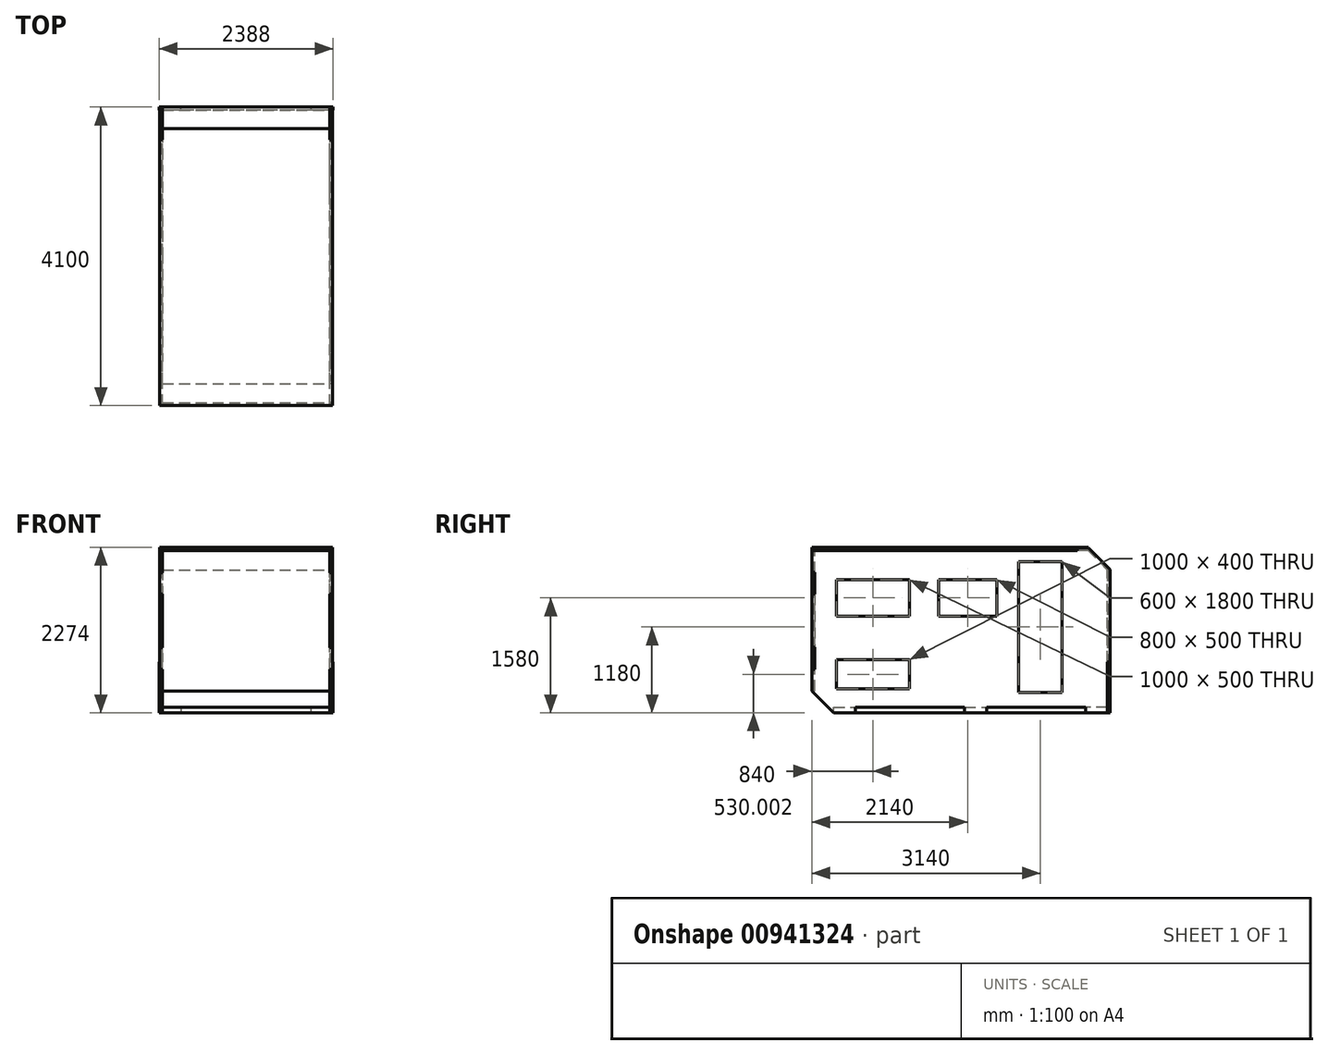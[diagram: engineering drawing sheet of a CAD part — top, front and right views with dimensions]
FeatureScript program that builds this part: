
annotation { "Feature Type Name" : "Feature", "Feature Type Description" : "" }
export const myFeature = defineFeature(function(context is Context, id is Id, definition is map)
    precondition{}
    {
        {
            var Q0;
            Q0=qCreatedBy(makeId("Front.planeOp"),FACE);
            var sketch = newSketch(context, id + "F0", { "sketchPlane" : qUnion([Q0])});
            skLineSegment(sketch, "E0", {"start": v(2175.17, -88.34) * mm, "end": v(1875.17, -88.34) * mm});
            skLineSegment(sketch, "E1", {"start": v(1875.17, -88.34) * mm, "end": v(1875.17, -8.34) * mm});
            skLineSegment(sketch, "E2", {"start": v(1875.17, -8.34) * mm, "end": v(87.17, -8.34) * mm});
            skLineSegment(sketch, "E3", {"start": v(87.17, -8.34) * mm, "end": v(87.17, -88.34) * mm});
            skLineSegment(sketch, "E4", {"start": v(87.17, -88.34) * mm, "end": v(-212.83, -88.34) * mm});
            skLineSegment(sketch, "E5", {"start": v(-212.83, -88.34) * mm, "end": v(-212.83, 611.66) * mm});
            skLineSegment(sketch, "E6", {"start": v(-212.83, 611.66) * mm, "end": v(-168.83, 611.66) * mm});
            skLineSegment(sketch, "E7", {"start": v(-168.83, 611.66) * mm, "end": v(-168.83, 1871.66) * mm});
            skLineSegment(sketch, "E8", {"start": v(2175.17, 611.66) * mm, "end": v(2131.17, 611.66) * mm});
            skLineSegment(sketch, "E9", {"start": v(2131.17, 1871.66) * mm, "end": v(2131.17, 611.66) * mm});
            skLineSegment(sketch, "E10", {"start": v(2175.17, -88.34) * mm, "end": v(2175.17, 611.66) * mm});
            skLineSegment(sketch, "E11", {"start": v(-168.83, 1871.66) * mm, "end": v(2131.17, 1871.66) * mm});
            skSolve(sketch);
        }
        {
            var Q0;
            Q0=makeQuery(id+"F0.imprint","IMPRINT",FACE,{"disambiguationData":[TD([[makeQuery(id+"F0.imprint","IMPRINT",EDGE,{"derivedFrom":sQuery(id+"F0.wireOp",EDGE,"E0")}),-1.0]])]});
            extrude(context, id + "F1", {"entities" : qUnion([Q0]), "depth" : 40 * mm, "offsetDistance" : 25 * mm});
        }
        {
            var Q0;
            Q0=makeQuery(id+"F1.opExtrude","SWEPT_FACE",FACE,{"disambiguationData":[OSD([sQuery(id+"F0.wireOp",EDGE,"E9")])]});
            var sketch = newSketch(context, id + "F2", { "sketchPlane" : qUnion([Q0])});
            skLineSegment(sketch, "E12", {"start": v(-40, -88.34) * mm, "end": v(-340, -88.34) * mm});
            skLineSegment(sketch, "E13", {"start": v(-340, -88.34) * mm, "end": v(-340, -8.34) * mm});
            skLineSegment(sketch, "E14", {"start": v(-340, -8.34) * mm, "end": v(-1700, -8.34) * mm});
            skLineSegment(sketch, "E15", {"start": v(-1700, -8.34) * mm, "end": v(-1700, -88.34) * mm});
            skLineSegment(sketch, "E16", {"start": v(-1700, -88.34) * mm, "end": v(-2000, -88.34) * mm});
            skLineSegment(sketch, "E17", {"start": v(-2000, -88.34) * mm, "end": v(-2000, -8.34) * mm});
            skLineSegment(sketch, "E18", {"start": v(-2000, -8.34) * mm, "end": v(-3500, -8.34) * mm});
            skLineSegment(sketch, "E19", {"start": v(-3500, -8.34) * mm, "end": v(-3500, -88.34) * mm});
            skLineSegment(sketch, "E20", {"start": v(-4100, 511.66) * mm, "end": v(-4060, 511.66) * mm});
            skLineSegment(sketch, "E21", {"start": v(-4060, 1841.66) * mm, "end": v(-4100, 1841.66) * mm});
            skLineSegment(sketch, "E22", {"start": v(-4100, 1841.66) * mm, "end": v(-4100, 2141.66) * mm});
            skLineSegment(sketch, "E23", {"start": v(-40, -88.34) * mm, "end": v(240.99, -88.34) * mm, "construction": true});
            skLineSegment(sketch, "E24", {"start": v(-4100, 2141.66) * mm, "end": v(-450, 2141.66) * mm});
            skLineSegment(sketch, "E25", {"start": v(0, 1881.66) * mm, "end": v(0, 613.66) * mm});
            skLineSegment(sketch, "E26", {"start": v(0, 613.66) * mm, "end": v(-40, 613.66) * mm});
            skLineSegment(sketch, "E27", {"start": v(0, 611.66) * mm, "end": v(0, 613.66) * mm, "construction": true});
            skLineSegment(sketch, "E28", {"start": v(-40, -88.34) * mm, "end": v(-40, 613.66) * mm});
            skLineSegment(sketch, "E29", {"start": v(-450, 2141.66) * mm, "end": v(-450, 2181.66) * mm});
            skLineSegment(sketch, "E30", {"start": v(-450, 2181.66) * mm, "end": v(-300, 2181.66) * mm});
            skLineSegment(sketch, "E31", {"start": v(-300, 2181.66) * mm, "end": v(0, 1881.66) * mm});
            skLineSegment(sketch, "E32", {"start": v(-4060, 511.66) * mm, "end": v(-4060, 811.66) * mm});
            skLineSegment(sketch, "E33", {"start": v(-4060, 811.66) * mm, "end": v(-4100, 811.66) * mm});
            skLineSegment(sketch, "E34", {"start": v(-4100, 811.66) * mm, "end": v(-4100, 1541.66) * mm});
            skLineSegment(sketch, "E35", {"start": v(-4100, 1541.66) * mm, "end": v(-4060, 1541.66) * mm});
            skLineSegment(sketch, "E36", {"start": v(-4060, 1541.66) * mm, "end": v(-4060, 1841.66) * mm});
            skLineSegment(sketch, "E37", {"start": v(-4100, 511.66) * mm, "end": v(-4100, 211.66) * mm});
            skLineSegment(sketch, "E38", {"start": v(-4100, 211.66) * mm, "end": v(-3800, -88.34) * mm});
            skLineSegment(sketch, "E39", {"start": v(-3800, -88.34) * mm, "end": v(-3500, -88.34) * mm});
            skSolve(sketch);
        }
        {
            var Q0;
            Q0 = qSketchRegion(id + "F2", true);
            extrude(context, id + "F3", {"entities" : qUnion([Q0]), "depth" : 40 * mm, "offsetDistance" : 25 * mm});
        }
        {
            var Q0;
            Q0=makeQuery(id+"F3.opExtrude","SWEPT_BODY",BODY,{"disambiguationData":[OSD([sQuery(id+"F2.wireOp",EDGE,"Dx9VQJn6-FMWb-czKo-p2x8-5996i8ps6jiw"),sQuery(id+"F2.wireOp",EDGE,"iBr2kLTf-II4E-46C1-aWTl-coTJPnEUG7vg"),sQuery(id+"F2.wireOp",EDGE,"E12"),sQuery(id+"F2.wireOp",EDGE,"E13"),sQuery(id+"F2.wireOp",EDGE,"E14"),sQuery(id+"F2.wireOp",EDGE,"E15"),sQuery(id+"F2.wireOp",EDGE,"E16"),sQuery(id+"F2.wireOp",EDGE,"E17"),sQuery(id+"F2.wireOp",EDGE,"E18"),sQuery(id+"F2.wireOp",EDGE,"E19"),sQuery(id+"F2.wireOp",EDGE,"i5OLA9vg-au1d-X7FX-vqS9-uq20iDOCNhxV"),sQuery(id+"F2.wireOp",EDGE,"lFKSZAOk-1tn5-VFxN-OIR4-CBnO5D4CmxQ9"),sQuery(id+"F2.wireOp",EDGE,"9CJDN3AS-R1GF-XZsS-VdxX-vJ2UmA5RAPMb"),sQuery(id+"F2.wireOp",EDGE,"E20"),sQuery(id+"F2.wireOp",EDGE,"zD5b52qF-HAvl-YPxf-Y24a-cu22lGjuYtzl"),sQuery(id+"F2.wireOp",EDGE,"E21"),sQuery(id+"F2.wireOp",EDGE,"E22"),sQuery(id+"F2.wireOp",EDGE,"iXH0r6w2-kwi5-uUCv-BWjB-DJfsQ7Iwdtw2"),sQuery(id+"F2.wireOp",EDGE,"QpDW6zXu-dsD6-1IIW-vLTo-eyrbGNoiJBE3"),sQuery(id+"F2.wireOp",EDGE,"iUTOi6hL-Xfo9-WyTo-EbXQ-NfrtJTtjvE0l"),sQuery(id+"F2.wireOp",EDGE,"k4gPe0jW-PS0o-5Mzn-7L7B-s2UWgm9pVnk1")])]});
            var Q1;
            Q1=makeQuery(id+"F1.opExtrude","CAP_EDGE",EDGE,{"disambiguationData":[OSD([sQuery(id+"F0.wireOp",EDGE,"mSf1c5Bj-CDj9-HMWg-OeSo-LXLhP5kgHdOP")])],"isStart":false});
            var Q2;
            Q2=makeQuery(id+"F1.opExtrude","CAP_EDGE",EDGE,{"disambiguationData":[OSD([sQuery(id+"F0.wireOp",EDGE,"E11")])],"isStart":false});
            transform(context, id + "F4", {"entities" : qUnion([Q0]), "transformType" : TransformType.TRANSLATION_DISTANCE, "transformDirection" : qUnion([Q2]), "distance" : 2340 * mm, "oppositeDirection" : true, "makeCopy" : true});
        }
        {
            var Q0;
            Q0=makeQuery(id+"F3.opExtrude","SWEPT_FACE",FACE,{"disambiguationData":[OSD([sQuery(id+"F2.wireOp",EDGE,"E36")])]});
            var sketch = newSketch(context, id + "F5", { "sketchPlane" : qUnion([Q0])});
            skLineSegment(sketch, "E40", {"start": v(2171.17, 1836.66) * mm, "end": v(2171.17, 1541.66) * mm});
            skLineSegment(sketch, "E41", {"start": v(2171.17, 1541.66) * mm, "end": v(2131.17, 1541.66) * mm});
            skLineSegment(sketch, "E42", {"start": v(2131.17, 1541.66) * mm, "end": v(2131.17, 806.66) * mm});
            skLineSegment(sketch, "E43", {"start": v(2131.17, 806.66) * mm, "end": v(2171.17, 806.66) * mm});
            skLineSegment(sketch, "E44", {"start": v(2171.17, 806.66) * mm, "end": v(2171.17, 511.66) * mm});
            skLineSegment(sketch, "E45", {"start": v(2171.17, 511.66) * mm, "end": v(2131.17, 511.66) * mm});
            skLineSegment(sketch, "E46", {"start": v(2131.17, 511.66) * mm, "end": v(2131.17, 211.66) * mm});
            skLineSegment(sketch, "E47", {"start": v(2131.17, 211.66) * mm, "end": v(-168.83, 211.66) * mm});
            skLineSegment(sketch, "E48", {"start": v(-168.83, 211.66) * mm, "end": v(-168.83, 511.66) * mm});
            skLineSegment(sketch, "E49", {"start": v(-168.83, 511.66) * mm, "end": v(-208.83, 511.66) * mm});
            skLineSegment(sketch, "E50", {"start": v(-208.83, 511.66) * mm, "end": v(-208.83, 806.66) * mm});
            skLineSegment(sketch, "E51", {"start": v(-208.83, 806.66) * mm, "end": v(-168.83, 806.66) * mm});
            skLineSegment(sketch, "E52", {"start": v(-168.83, 806.66) * mm, "end": v(-168.83, 1541.66) * mm});
            skLineSegment(sketch, "E53", {"start": v(-168.83, 1541.66) * mm, "end": v(-208.83, 1541.66) * mm});
            skLineSegment(sketch, "E54", {"start": v(-208.83, 1541.66) * mm, "end": v(-208.83, 1836.66) * mm});
            skLineSegment(sketch, "E55", {"start": v(-208.83, 1836.66) * mm, "end": v(-168.83, 1836.66) * mm});
            skLineSegment(sketch, "E56", {"start": v(-168.83, 1836.66) * mm, "end": v(-168.83, 2141.66) * mm});
            skLineSegment(sketch, "E57", {"start": v(-168.83, 2141.66) * mm, "end": v(2131.17, 2141.66) * mm});
            skLineSegment(sketch, "E58", {"start": v(2131.17, 2141.66) * mm, "end": v(2131.17, 1836.66) * mm});
            skLineSegment(sketch, "E59", {"start": v(2131.17, 1836.66) * mm, "end": v(2171.17, 1836.66) * mm});
            skSolve(sketch);
        }
        {
            var Q0;
            Q0 = qSketchRegion(id + "F5", true);
            extrude(context, id + "F6", {"entities" : qUnion([Q0]), "depth" : 40 * mm, "offsetDistance" : 25 * mm});
        }
        {
            var Q0;
            Q0=makeQuery(id+"F4.opPattern","COPY",FACE,{"derivedFrom":makeQuery(id+"F3.opExtrude","SWEPT_FACE",FACE,{"disambiguationData":[OSD([sQuery(id+"F2.wireOp",EDGE,"E24")])]}),"instanceName":"1"});
            var sketch = newSketch(context, id + "F7", { "sketchPlane" : qUnion([Q0])});
            skLineSegment(sketch, "E60", {"start": v(-208.83, -4100) * mm, "end": v(-208.83, -450) * mm});
            skLineSegment(sketch, "E61", {"start": v(-208.83, -450) * mm, "end": v(-168.83, -450) * mm});
            skLineSegment(sketch, "E62", {"start": v(-168.83, -450) * mm, "end": v(-168.83, -300) * mm});
            skLineSegment(sketch, "E63", {"start": v(-168.83, -300) * mm, "end": v(2131.17, -300) * mm});
            skLineSegment(sketch, "E64", {"start": v(2131.17, -300) * mm, "end": v(2131.17, -450) * mm});
            skLineSegment(sketch, "E65", {"start": v(2131.17, -450) * mm, "end": v(2171.17, -450) * mm});
            skLineSegment(sketch, "E66", {"start": v(2171.17, -450) * mm, "end": v(2171.17, -4100) * mm});
            skLineSegment(sketch, "E67", {"start": v(2171.17, -4100) * mm, "end": v(-208.83, -4100) * mm});
            skSolve(sketch);
        }
        {
            var Q0;
            Q0 = qSketchRegion(id + "F7", true);
            extrude(context, id + "F8", {"entities" : qUnion([Q0]), "depth" : 44 * mm, "offsetDistance" : 25 * mm});
        }
        {
            var Q0;
            Q0=makeQuery(id+"F3.opExtrude","CAP_FACE",FACE,{"disambiguationData":[OSD([sQuery(id+"F2.wireOp",EDGE,"E12"),sQuery(id+"F2.wireOp",EDGE,"E13"),sQuery(id+"F2.wireOp",EDGE,"E14"),sQuery(id+"F2.wireOp",EDGE,"E15"),sQuery(id+"F2.wireOp",EDGE,"E16"),sQuery(id+"F2.wireOp",EDGE,"E17"),sQuery(id+"F2.wireOp",EDGE,"E18"),sQuery(id+"F2.wireOp",EDGE,"E19"),sQuery(id+"F2.wireOp",EDGE,"i5OLA9vg-au1d-X7FX-vqS9-uq20iDOCNhxV"),sQuery(id+"F2.wireOp",EDGE,"lFKSZAOk-1tn5-VFxN-OIR4-CBnO5D4CmxQ9"),sQuery(id+"F2.wireOp",EDGE,"9CJDN3AS-R1GF-XZsS-VdxX-vJ2UmA5RAPMb"),sQuery(id+"F2.wireOp",EDGE,"E20"),sQuery(id+"F2.wireOp",EDGE,"E21"),sQuery(id+"F2.wireOp",EDGE,"E22"),sQuery(id+"F2.wireOp",EDGE,"E24"),sQuery(id+"F2.wireOp",EDGE,"E25"),sQuery(id+"F2.wireOp",EDGE,"E26"),sQuery(id+"F2.wireOp",EDGE,"E28"),sQuery(id+"F2.wireOp",EDGE,"E29"),sQuery(id+"F2.wireOp",EDGE,"E30"),sQuery(id+"F2.wireOp",EDGE,"E31"),sQuery(id+"F2.wireOp",EDGE,"E32"),sQuery(id+"F2.wireOp",EDGE,"E33"),sQuery(id+"F2.wireOp",EDGE,"E34"),sQuery(id+"F2.wireOp",EDGE,"E35"),sQuery(id+"F2.wireOp",EDGE,"E36")])],"isStart":true});
            var sketch = newSketch(context, id + "F9", { "sketchPlane" : qUnion([Q0])});
            skLineSegment(sketch, "E68", {"start": v(300, 2181.66) * mm, "end": v(300, 2141.66) * mm});
            skLineSegment(sketch, "E69", {"start": v(300, 2141.66) * mm, "end": v(38.7, 1871.66) * mm});
            skLineSegment(sketch, "E70", {"start": v(38.7, 1871.66) * mm, "end": v(0, 1871.66) * mm});
            skLineSegment(sketch, "E71", {"start": v(0, 1871.66) * mm, "end": v(300, 2181.66) * mm});
            skSolve(sketch);
        }
        {
            var Q0;
            Q0 = qSketchRegion(id + "F9", true);
            var Q1;
            Q1=makeQuery(id+"F4.opPattern","COPY",BODY,{"derivedFrom":makeQuery(id+"F3.opExtrude","SWEPT_BODY",BODY,{"disambiguationData":[OSD([sQuery(id+"F2.wireOp",EDGE,"E12"),sQuery(id+"F2.wireOp",EDGE,"E13"),sQuery(id+"F2.wireOp",EDGE,"E14"),sQuery(id+"F2.wireOp",EDGE,"E15"),sQuery(id+"F2.wireOp",EDGE,"E16"),sQuery(id+"F2.wireOp",EDGE,"E17"),sQuery(id+"F2.wireOp",EDGE,"E18"),sQuery(id+"F2.wireOp",EDGE,"E19"),sQuery(id+"F2.wireOp",EDGE,"i5OLA9vg-au1d-X7FX-vqS9-uq20iDOCNhxV"),sQuery(id+"F2.wireOp",EDGE,"9CJDN3AS-R1GF-XZsS-VdxX-vJ2UmA5RAPMb"),sQuery(id+"F2.wireOp",EDGE,"E20"),sQuery(id+"F2.wireOp",EDGE,"E21"),sQuery(id+"F2.wireOp",EDGE,"E22"),sQuery(id+"F2.wireOp",EDGE,"E24"),sQuery(id+"F2.wireOp",EDGE,"E25"),sQuery(id+"F2.wireOp",EDGE,"E26"),sQuery(id+"F2.wireOp",EDGE,"E28"),sQuery(id+"F2.wireOp",EDGE,"E29"),sQuery(id+"F2.wireOp",EDGE,"E30"),sQuery(id+"F2.wireOp",EDGE,"E31"),sQuery(id+"F2.wireOp",EDGE,"E32"),sQuery(id+"F2.wireOp",EDGE,"E33"),sQuery(id+"F2.wireOp",EDGE,"E34"),sQuery(id+"F2.wireOp",EDGE,"E35"),sQuery(id+"F2.wireOp",EDGE,"E36")])]}),"instanceName":"1"});
            extrude(context, id + "F10", {"entities" : qUnion([Q0]), "endBound" : BoundingType.UP_TO_BODY, "depth" : 250 * mm, "endBoundEntityBody" : qUnion([Q1]), "offsetDistance" : 25 * mm});
        }
        {
            var Q0;
            Q0=makeQuery(id+"F3.opExtrude","SWEPT_FACE",FACE,{"disambiguationData":[OSD([sQuery(id+"F2.wireOp",EDGE,"E18")])]});
            var sketch = newSketch(context, id + "F11", { "sketchPlane" : qUnion([Q0])});
            skLineSegment(sketch, "E72", {"start": v(2131.17, 3800) * mm, "end": v(2131.17, 3500) * mm});
            skLineSegment(sketch, "E73", {"start": v(2131.17, 3500) * mm, "end": v(2171.17, 3500) * mm});
            skLineSegment(sketch, "E74", {"start": v(2171.17, 3500) * mm, "end": v(2171.17, 2000) * mm});
            skLineSegment(sketch, "E75", {"start": v(2171.17, 2000) * mm, "end": v(2131.17, 2000) * mm});
            skLineSegment(sketch, "E76", {"start": v(2131.17, 2000) * mm, "end": v(2131.17, 1700) * mm});
            skLineSegment(sketch, "E77", {"start": v(2131.17, 1700) * mm, "end": v(2171.17, 1700) * mm});
            skLineSegment(sketch, "E78", {"start": v(2171.17, 1700) * mm, "end": v(2171.17, 340) * mm});
            skLineSegment(sketch, "E79", {"start": v(2131.17, 340) * mm, "end": v(2131.17, 40) * mm});
            skLineSegment(sketch, "E80", {"start": v(2131.17, 40) * mm, "end": v(1875.17, 40) * mm});
            skLineSegment(sketch, "E81", {"start": v(1875.17, 40) * mm, "end": v(1875.17, 0) * mm});
            skLineSegment(sketch, "E82", {"start": v(1875.17, 0) * mm, "end": v(87.17, 0) * mm});
            skLineSegment(sketch, "E83", {"start": v(87.17, 0) * mm, "end": v(87.17, 40) * mm});
            skLineSegment(sketch, "E84", {"start": v(87.17, 40) * mm, "end": v(-168.83, 40) * mm});
            skLineSegment(sketch, "E85", {"start": v(-168.83, 40) * mm, "end": v(-168.83, 340) * mm});
            skLineSegment(sketch, "E86", {"start": v(2171.17, 340) * mm, "end": v(2131.17, 340) * mm});
            skLineSegment(sketch, "E87", {"start": v(-168.83, 340) * mm, "end": v(-208.83, 340) * mm});
            skLineSegment(sketch, "E88", {"start": v(-208.83, 340) * mm, "end": v(-208.83, 1700) * mm});
            skLineSegment(sketch, "E89", {"start": v(-208.83, 1700) * mm, "end": v(-168.83, 1700) * mm});
            skLineSegment(sketch, "E90", {"start": v(-168.83, 1700) * mm, "end": v(-168.83, 2000) * mm});
            skLineSegment(sketch, "E91", {"start": v(-168.83, 2000) * mm, "end": v(-208.83, 2000) * mm});
            skLineSegment(sketch, "E92", {"start": v(-208.83, 2000) * mm, "end": v(-208.83, 3500) * mm});
            skLineSegment(sketch, "E93", {"start": v(-208.83, 3500) * mm, "end": v(-168.83, 3500) * mm});
            skLineSegment(sketch, "E94", {"start": v(-168.83, 3500) * mm, "end": v(-168.83, 3800) * mm});
            skLineSegment(sketch, "E95", {"start": v(-168.83, 3800) * mm, "end": v(2131.17, 3800) * mm});
            skSolve(sketch);
        }
        {
            var Q0;
            Q0 = qSketchRegion(id + "F11", true);
            extrude(context, id + "F12", {"entities" : qUnion([Q0]), "depth" : 80 * mm, "offsetDistance" : 25 * mm});
        }
        {
            var Q0;
            Q0=makeQuery(id+"F3.opExtrude","CAP_FACE",FACE,{"disambiguationData":[OSD([sQuery(id+"F2.wireOp",EDGE,"E12"),sQuery(id+"F2.wireOp",EDGE,"E13"),sQuery(id+"F2.wireOp",EDGE,"E14"),sQuery(id+"F2.wireOp",EDGE,"E15"),sQuery(id+"F2.wireOp",EDGE,"E16"),sQuery(id+"F2.wireOp",EDGE,"E17"),sQuery(id+"F2.wireOp",EDGE,"E18"),sQuery(id+"F2.wireOp",EDGE,"E19"),sQuery(id+"F2.wireOp",EDGE,"i5OLA9vg-au1d-X7FX-vqS9-uq20iDOCNhxV"),sQuery(id+"F2.wireOp",EDGE,"9CJDN3AS-R1GF-XZsS-VdxX-vJ2UmA5RAPMb"),sQuery(id+"F2.wireOp",EDGE,"E20"),sQuery(id+"F2.wireOp",EDGE,"E21"),sQuery(id+"F2.wireOp",EDGE,"E22"),sQuery(id+"F2.wireOp",EDGE,"E24"),sQuery(id+"F2.wireOp",EDGE,"E25"),sQuery(id+"F2.wireOp",EDGE,"E26"),sQuery(id+"F2.wireOp",EDGE,"E28"),sQuery(id+"F2.wireOp",EDGE,"E29"),sQuery(id+"F2.wireOp",EDGE,"E30"),sQuery(id+"F2.wireOp",EDGE,"E31"),sQuery(id+"F2.wireOp",EDGE,"E32"),sQuery(id+"F2.wireOp",EDGE,"E33"),sQuery(id+"F2.wireOp",EDGE,"E34"),sQuery(id+"F2.wireOp",EDGE,"E35"),sQuery(id+"F2.wireOp",EDGE,"E36")])],"isStart":false});
            var sketch = newSketch(context, id + "F13", { "sketchPlane" : qUnion([Q0])});
            skLineSegment(sketch, "E96.bottom", {"start": v(-3760, 1741.66) * mm, "end": v(-2760, 1741.66) * mm});
            skLineSegment(sketch, "E96.top", {"start": v(-3760, 1241.66) * mm, "end": v(-2760, 1241.66) * mm});
            skLineSegment(sketch, "E96.left", {"start": v(-3760, 1741.66) * mm, "end": v(-3760, 1241.66) * mm});
            skLineSegment(sketch, "E96.right", {"start": v(-2760, 1741.66) * mm, "end": v(-2760, 1241.66) * mm});
            skLineSegment(sketch, "E97.bottom", {"start": v(-2360, 1741.66) * mm, "end": v(-1560, 1741.66) * mm});
            skLineSegment(sketch, "E97.top", {"start": v(-2360, 1241.66) * mm, "end": v(-1560, 1241.66) * mm});
            skLineSegment(sketch, "E97.left", {"start": v(-2360, 1741.66) * mm, "end": v(-2360, 1241.66) * mm});
            skLineSegment(sketch, "E97.right", {"start": v(-1560, 1741.66) * mm, "end": v(-1560, 1241.66) * mm});
            skLineSegment(sketch, "E98.bottom", {"start": v(-660, 191.66) * mm, "end": v(-1260, 191.66) * mm});
            skLineSegment(sketch, "E98.top", {"start": v(-660, 1991.66) * mm, "end": v(-1260, 1991.66) * mm});
            skLineSegment(sketch, "E98.left", {"start": v(-660, 191.66) * mm, "end": v(-660, 1991.66) * mm});
            skLineSegment(sketch, "E98.right", {"start": v(-1260, 191.66) * mm, "end": v(-1260, 1991.66) * mm});
            skLineSegment(sketch, "E99.bottom", {"start": v(-3760, 641.66) * mm, "end": v(-2760, 641.66) * mm});
            skLineSegment(sketch, "E99.top", {"start": v(-3760, 241.66) * mm, "end": v(-2760, 241.66) * mm});
            skLineSegment(sketch, "E99.left", {"start": v(-3760, 641.66) * mm, "end": v(-3760, 241.66) * mm});
            skLineSegment(sketch, "E99.right", {"start": v(-2760, 641.66) * mm, "end": v(-2760, 241.66) * mm});
            skSolve(sketch);
        }
        {
            var Q0;
            Q0 = qSketchRegion(id + "F13", true);
            extrude(context, id + "F14", {"entities" : qUnion([Q0]), "operationType" : NewBodyOperationType.REMOVE, "endBound" : BoundingType.UP_TO_NEXT, "oppositeDirection" : true, "depth" : 25 * mm, "offsetDistance" : 25 * mm});
        }
    });
